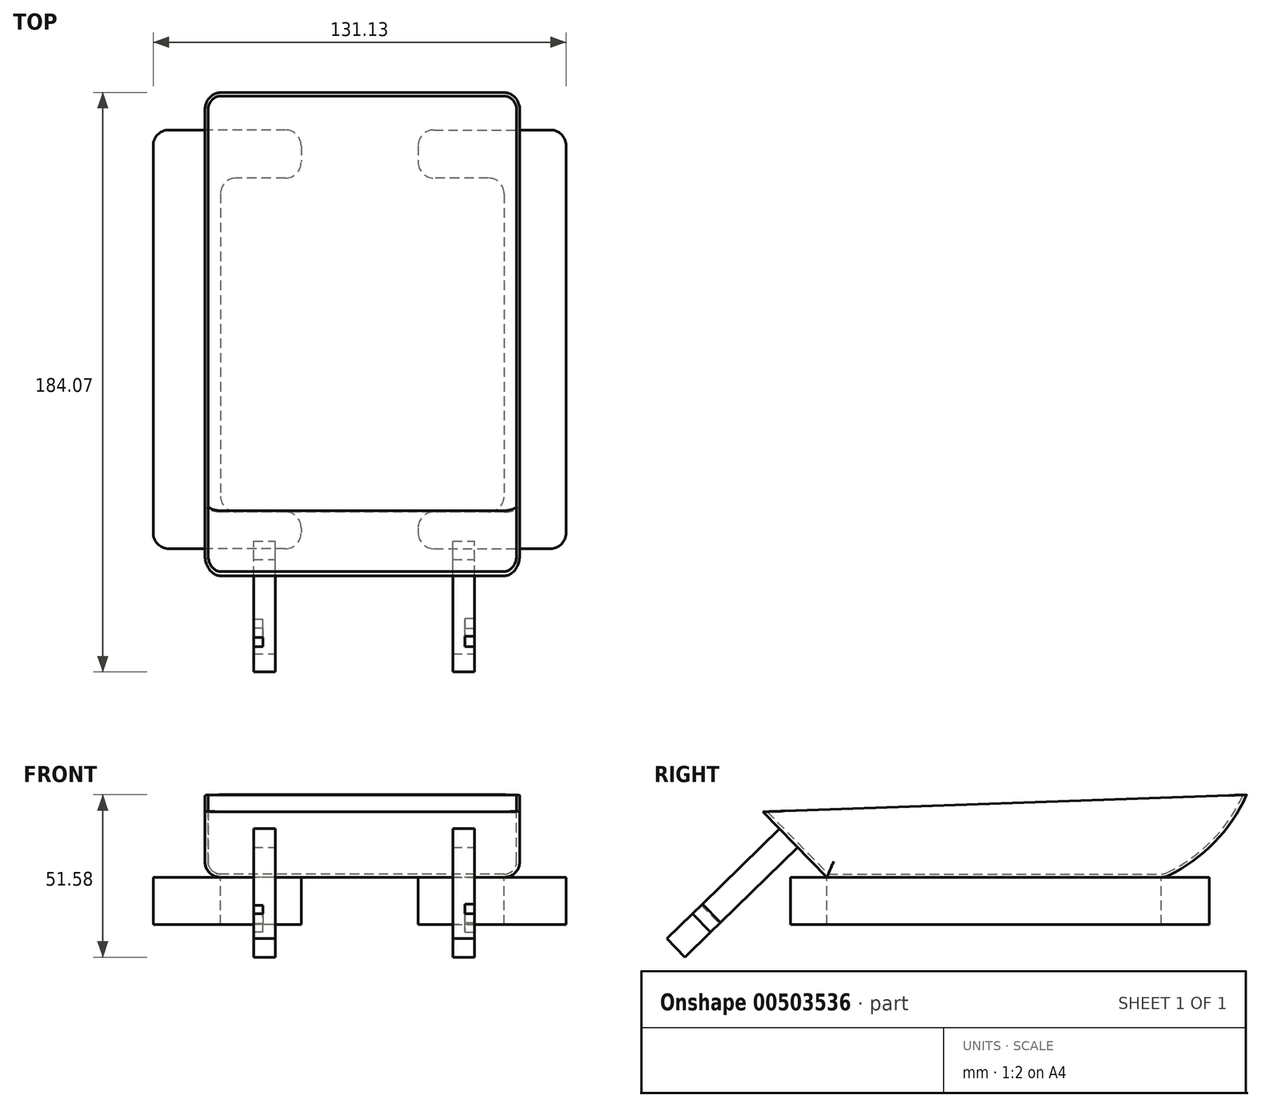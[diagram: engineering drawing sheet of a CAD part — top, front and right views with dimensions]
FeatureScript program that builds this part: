
annotation { "Feature Type Name" : "Feature", "Feature Type Description" : "" }
export const myFeature = defineFeature(function(context is Context, id is Id, definition is map)
    precondition{}
    {
        {
            var Q0;
            Q0=qCreatedBy(makeId("Right.planeOp"),FACE);
            var sketch = newSketch(context, id + "F0", { "sketchPlane" : qUnion([Q0])});
            skLineSegment(sketch, "E0", {"start": v(43.87, 0) * mm, "end": v(-62.22, 0) * mm});
            skLineSegment(sketch, "E1", {"start": v(-62.22, 0) * mm, "end": v(-82.51, 20.8) * mm});
            skArc(sketch, "E2", {"start": v(46.03, 0.49) * mm, "mid": v(60.82, 11.11) * mm, "end": v(71.02, 26.2) * mm});
            skPoint(sketch, "E3.visualSharp", {"position": v(44.98, 0) * mm});
            skArc(sketch, "E3.filletArc", {"start": v(43.87, 0) * mm, "mid": v(44.98, 0.12) * mm, "end": v(46.03, 0.49) * mm});
            skPoint(sketch, "E4.start.orphan", {"position": v(43.87, 3.2) * mm});
            skLineSegment(sketch, "E5", {"start": v(-82.51, 20.8) * mm, "end": v(71.02, 26.2) * mm});
            skSolve(sketch);
        }
        {
            var Q0;
            Q0=makeQuery(id+"F0.imprint","IMPRINT",FACE,{"disambiguationData":[TD([[makeQuery(id+"F0.imprint","IMPRINT",EDGE,{"derivedFrom":sQuery(id+"F0.wireOp",EDGE,"E0")}),-1.0]])]});
            extrude(context, id + "F1", {"entities" : qUnion([Q0]), "depth" : 100 * mm});
        }
        {
            var Q0;
            Q0=makeQuery(id+"F1.opExtrude","CAP_EDGE",EDGE,{"disambiguationData":[OSD([sQuery(id+"F0.wireOp",EDGE,"E1")])],"isStart":false});
            var Q1;
            Q1=makeQuery(id+"F1.opExtrude","CAP_EDGE",EDGE,{"disambiguationData":[OSD([sQuery(id+"F0.wireOp",EDGE,"E0")])],"isStart":false});
            var Q2;
            Q2=makeQuery(id+"F1.opExtrude","CAP_EDGE",EDGE,{"disambiguationData":[OSD([sQuery(id+"F0.wireOp",EDGE,"E2")])],"isStart":true});
            var Q3;
            Q3=makeQuery(id+"F1.opExtrude","CAP_EDGE",EDGE,{"disambiguationData":[OSD([sQuery(id+"F0.wireOp",EDGE,"E1")])],"isStart":true});
            fillet(context, id + "F2", {"entities" : qUnion([Q0, Q1, Q2, Q3]), "radius" : 5 * mm, "tangentPropagation" : true, "allowEdgeOverflow" : false});
        }
        {
            var Q0;
            Q0=makeQuery(id+"F1.opExtrude","SWEPT_FACE",FACE,{"disambiguationData":[OSD([sQuery(id+"F0.wireOp",EDGE,"E5")])]});
            shell(context, id + "F3", {"entities" : qUnion([Q0]), "thickness" : 1 * mm});
        }
        {
            var Q0;
            Q0=makeQuery(id+"F1.opExtrude","SWEPT_FACE",FACE,{"disambiguationData":[OSD([sQuery(id+"F0.wireOp",EDGE,"E0")])]});
            var sketch = newSketch(context, id + "F4", { "sketchPlane" : qUnion([Q0])});
            skLineSegment(sketch, "E6.bottom", {"start": v(30.57, -59.13) * mm, "end": v(-16.43, -59.13) * mm});
            skLineSegment(sketch, "E6.top", {"start": v(30.57, 73.87) * mm, "end": v(-16.43, 73.87) * mm});
            skLineSegment(sketch, "E6.left", {"start": v(30.57, -59.13) * mm, "end": v(30.57, 73.87) * mm});
            skLineSegment(sketch, "E6.right", {"start": v(-16.43, -59.13) * mm, "end": v(-16.43, 73.87) * mm});
            skLineSegment(sketch, "E7.bottom", {"start": v(67.7, -59.13) * mm, "end": v(114.7, -59.13) * mm});
            skLineSegment(sketch, "E7.top", {"start": v(67.7, 73.87) * mm, "end": v(114.7, 73.87) * mm});
            skLineSegment(sketch, "E7.left", {"start": v(67.7, -59.13) * mm, "end": v(67.7, 73.87) * mm});
            skLineSegment(sketch, "E7.right", {"start": v(114.7, -59.13) * mm, "end": v(114.7, 73.87) * mm});
            skSolve(sketch);
        }
        {
            var Q0;
            {var subQ5=sQuery(id+"F4.wireOp",EDGE,"E7.bottom");Q0=makeQuery(id+"F4.imprint","IMPRINT",FACE,{"disambiguationData":[TD([[makeQuery(id+"F4.imprint","IMPRINT",EDGE,{"derivedFrom":subQ5}),1.0]])]});}
            var Q1;
            {var subQ5=sQuery(id+"F4.wireOp",EDGE,"E6.bottom");Q1=makeQuery(id+"F4.imprint","IMPRINT",FACE,{"disambiguationData":[TD([[makeQuery(id+"F4.imprint","IMPRINT",EDGE,{"derivedFrom":subQ5}),-1.0]])]});}
            extrude(context, id + "F5", {"entities" : qUnion([Q0, Q1]), "depth" : 15 * mm});
        }
        {
            var Q0;
            Q0=makeQuery(id+"F5.opExtrude","SWEPT_EDGE",EDGE,{"disambiguationData":[OSD([sQuery(id+"F4.wireOp",EDGE,"E7.top"),sQuery(id+"F4.wireOp",EDGE,"E7.right")])]});
            var Q1;
            Q1=makeQuery(id+"F5.opExtrude","SWEPT_EDGE",EDGE,{"disambiguationData":[OSD([sQuery(id+"F4.wireOp",EDGE,"E7.bottom"),sQuery(id+"F4.wireOp",EDGE,"E7.right")])]});
            var Q2;
            Q2=makeQuery(id+"F5.opExtrude","SWEPT_EDGE",EDGE,{"disambiguationData":[OSD([sQuery(id+"F4.wireOp",EDGE,"E6.top"),sQuery(id+"F4.wireOp",EDGE,"E6.right")])]});
            var Q3;
            Q3=makeQuery(id+"F5.opExtrude","SWEPT_EDGE",EDGE,{"disambiguationData":[OSD([sQuery(id+"F4.wireOp",EDGE,"E6.bottom"),sQuery(id+"F4.wireOp",EDGE,"E6.right")])]});
            var Q4;
            Q4=makeQuery(id+"F5.opExtrude","SWEPT_EDGE",EDGE,{"disambiguationData":[OSD([sQuery(id+"F4.wireOp",EDGE,"E6.bottom"),sQuery(id+"F4.wireOp",EDGE,"E6.left")])]});
            var Q5;
            Q5=makeQuery(id+"F5.opExtrude","SWEPT_EDGE",EDGE,{"disambiguationData":[OSD([sQuery(id+"F4.wireOp",EDGE,"E7.bottom"),sQuery(id+"F4.wireOp",EDGE,"E7.left")])]});
            var Q6;
            Q6=makeQuery(id+"F5.opExtrude","SWEPT_EDGE",EDGE,{"disambiguationData":[OSD([sQuery(id+"F4.wireOp",EDGE,"E6.top"),sQuery(id+"F4.wireOp",EDGE,"E6.left")])]});
            var Q7;
            Q7=makeQuery(id+"F5.opExtrude","SWEPT_EDGE",EDGE,{"disambiguationData":[OSD([sQuery(id+"F4.wireOp",EDGE,"E7.top"),sQuery(id+"F4.wireOp",EDGE,"E7.left")])]});
            var Q8;
            {var subQ0=sQuery(id+"F0.wireOp",EDGE,"E0");var subQ1=sQuery(id+"F0.wireOp",EDGE,"E1");Q8=makeQuery(id+"F5.opExtrude","SWEPT_EDGE",EDGE,{"disambiguationData":[OSD([subQ0,subQ1]),TDD([makeQuery(id+"F4.imprint","INTERSECT",VERTEX,{"derivedFrom":[makeQuery(id+"F1.opExtrude","SWEPT_EDGE",EDGE,{"disambiguationData":[OSD([subQ0,subQ1])]}),makeQuery(id+"F2.opFillet","BLEND_EDGE",EDGE,{"blendedFrom":[makeQuery(id+"F1.opExtrude","CAP_EDGE",EDGE,{"disambiguationData":[OSD([subQ0])],"isStart":true}),makeQuery(id+"F1.opExtrude","SWEPT_FACE",FACE,{"disambiguationData":[OSD([subQ0])]})],"blendedInto":[makeQuery(id+"F1.opExtrude","SWEPT_FACE",FACE,{"disambiguationData":[OSD([subQ0])]})]})]})])]});}
            var Q9;
            {var subQ0=sQuery(id+"F0.wireOp",EDGE,"E0");var subQ1=sQuery(id+"F0.wireOp",EDGE,"E1");Q9=makeQuery(id+"F5.opExtrude","SWEPT_EDGE",EDGE,{"disambiguationData":[OSD([subQ0,subQ1]),TDD([makeQuery(id+"F4.imprint","INTERSECT",VERTEX,{"derivedFrom":[makeQuery(id+"F1.opExtrude","SWEPT_EDGE",EDGE,{"disambiguationData":[OSD([subQ0,subQ1])]}),makeQuery(id+"F2.opFillet","BLEND_EDGE",EDGE,{"blendedFrom":[makeQuery(id+"F1.opExtrude","CAP_EDGE",EDGE,{"disambiguationData":[OSD([subQ0])],"isStart":false}),makeQuery(id+"F1.opExtrude","SWEPT_FACE",FACE,{"disambiguationData":[OSD([subQ0])]})],"blendedInto":[makeQuery(id+"F1.opExtrude","SWEPT_FACE",FACE,{"disambiguationData":[OSD([subQ0])]})]})]})])]});}
            var Q10;
            {var subQ0=sQuery(id+"F0.wireOp",EDGE,"E0");var subQ1=sQuery(id+"F0.wireOp",EDGE,"E3.filletArc");Q10=makeQuery(id+"F5.opExtrude","SWEPT_EDGE",EDGE,{"disambiguationData":[OSD([subQ0,subQ1]),TDD([makeQuery(id+"F4.imprint","INTERSECT",VERTEX,{"derivedFrom":[makeQuery(id+"F1.opExtrude","SWEPT_EDGE",EDGE,{"disambiguationData":[OSD([subQ0,subQ1])]}),makeQuery(id+"F2.opFillet","BLEND_EDGE",EDGE,{"blendedFrom":[makeQuery(id+"F1.opExtrude","CAP_EDGE",EDGE,{"disambiguationData":[OSD([subQ0])],"isStart":true}),makeQuery(id+"F1.opExtrude","SWEPT_FACE",FACE,{"disambiguationData":[OSD([subQ0])]})],"blendedInto":[makeQuery(id+"F1.opExtrude","SWEPT_FACE",FACE,{"disambiguationData":[OSD([subQ0])]})]})]})])]});}
            var Q11;
            {var subQ0=sQuery(id+"F0.wireOp",EDGE,"E0");var subQ1=sQuery(id+"F0.wireOp",EDGE,"E3.filletArc");Q11=makeQuery(id+"F5.opExtrude","SWEPT_EDGE",EDGE,{"disambiguationData":[OSD([subQ0,subQ1]),TDD([makeQuery(id+"F4.imprint","INTERSECT",VERTEX,{"derivedFrom":[makeQuery(id+"F1.opExtrude","SWEPT_EDGE",EDGE,{"disambiguationData":[OSD([subQ0,subQ1])]}),makeQuery(id+"F2.opFillet","BLEND_EDGE",EDGE,{"blendedFrom":[makeQuery(id+"F1.opExtrude","CAP_EDGE",EDGE,{"disambiguationData":[OSD([subQ0])],"isStart":false}),makeQuery(id+"F1.opExtrude","SWEPT_FACE",FACE,{"disambiguationData":[OSD([subQ0])]})],"blendedInto":[makeQuery(id+"F1.opExtrude","SWEPT_FACE",FACE,{"disambiguationData":[OSD([subQ0])]})]})]})])]});}
            var Q12;
            Q12=makeQuery(id+"F5.opExtrude","SWEPT_EDGE",EDGE,{"disambiguationData":[OSD([sQuery(id+"F0.wireOp",EDGE,"E0"),sQuery(id+"F0.wireOp",EDGE,"E3.filletArc"),sQuery(id+"F4.wireOp",EDGE,"E7.left")])]});
            var Q13;
            Q13=makeQuery(id+"F5.opExtrude","SWEPT_EDGE",EDGE,{"disambiguationData":[OSD([sQuery(id+"F0.wireOp",EDGE,"E0"),sQuery(id+"F0.wireOp",EDGE,"E3.filletArc"),sQuery(id+"F4.wireOp",EDGE,"E6.left")])]});
            var Q14;
            Q14=makeQuery(id+"F5.opExtrude","SWEPT_EDGE",EDGE,{"disambiguationData":[OSD([sQuery(id+"F0.wireOp",EDGE,"E0"),sQuery(id+"F0.wireOp",EDGE,"E1"),sQuery(id+"F4.wireOp",EDGE,"E6.left")])]});
            var Q15;
            Q15=makeQuery(id+"F5.opExtrude","SWEPT_EDGE",EDGE,{"disambiguationData":[OSD([sQuery(id+"F0.wireOp",EDGE,"E0"),sQuery(id+"F0.wireOp",EDGE,"E1"),sQuery(id+"F4.wireOp",EDGE,"E7.left")])]});
            fillet(context, id + "F6", {"entities" : qUnion([Q0, Q1, Q2, Q3, Q4, Q5, Q6, Q7, Q8, Q9, Q10, Q11, Q12, Q13, Q14, Q15]), "radius" : 5 * mm, "tangentPropagation" : true, "allowEdgeOverflow" : false});
        }
        {
            var Q0;
            Q0=makeQuery(id+"F1.opExtrude","SWEPT_FACE",FACE,{"disambiguationData":[OSD([sQuery(id+"F0.wireOp",EDGE,"E1")])]});
            var sketch = newSketch(context, id + "F7", { "sketchPlane" : qUnion([Q0])});
            skLineSegment(sketch, "E8.bottom", {"start": v(15.46, 64.99) * mm, "end": v(22.3, 64.99) * mm});
            skLineSegment(sketch, "E8.top", {"start": v(15.46, 56.78) * mm, "end": v(22.3, 56.78) * mm});
            skLineSegment(sketch, "E8.left", {"start": v(15.46, 64.99) * mm, "end": v(15.46, 56.78) * mm});
            skLineSegment(sketch, "E8.right", {"start": v(22.3, 64.99) * mm, "end": v(22.3, 56.78) * mm});
            skPoint(sketch, "E8.middle", {"position": v(18.88, 60.89) * mm});
            skLineSegment(sketch, "E9.bottom", {"start": v(78.72, 64.99) * mm, "end": v(85.56, 64.99) * mm});
            skLineSegment(sketch, "E9.top", {"start": v(78.72, 56.78) * mm, "end": v(85.56, 56.78) * mm});
            skLineSegment(sketch, "E9.left", {"start": v(78.72, 64.99) * mm, "end": v(78.72, 56.78) * mm});
            skLineSegment(sketch, "E9.right", {"start": v(85.56, 64.99) * mm, "end": v(85.56, 56.78) * mm});
            skPoint(sketch, "E9.middle", {"position": v(82.14, 60.89) * mm});
            skSolve(sketch);
        }
        {
            var Q0;
            Q0=makeQuery(id+"F7.imprint","IMPRINT",FACE,{"disambiguationData":[TD([[makeQuery(id+"F7.imprint","IMPRINT",EDGE,{"derivedFrom":sQuery(id+"F7.wireOp",EDGE,"E8.bottom")}),-1.0]])]});
            var Q1;
            Q1=makeQuery(id+"F7.imprint","IMPRINT",FACE,{"disambiguationData":[TD([[makeQuery(id+"F7.imprint","IMPRINT",EDGE,{"derivedFrom":sQuery(id+"F7.wireOp",EDGE,"E9.bottom")}),-1.0]])]});
            extrude(context, id + "F8", {"entities" : qUnion([Q0, Q1]), "operationType" : NewBodyOperationType.ADD, "depth" : 50 * mm});
        }
        {
            var Q0;
            Q0=makeQuery(id+"F8.opExtrude","SWEPT_FACE",FACE,{"disambiguationData":[OSD([sQuery(id+"F7.wireOp",EDGE,"E9.right")])]});
            var sketch = newSketch(context, id + "F9", { "sketchPlane" : qUnion([Q0])});
            skLineSegment(sketch, "E10", {"start": v(-116.26, 0) * mm, "end": v(-91.52, -25.36) * mm});
            skLineSegment(sketch, "E11", {"start": v(-91.52, -25.36) * mm, "end": v(-88.32, -22.24) * mm});
            skLineSegment(sketch, "E12", {"start": v(-88.32, -22.24) * mm, "end": v(-111.31, 1.32) * mm});
            skLineSegment(sketch, "E13", {"start": v(-111.31, 1.32) * mm, "end": v(-116.26, 0) * mm});
            skSolve(sketch);
        }
        {
            var Q0;
            {var subQ0=sQuery(id+"F9.wireOp",EDGE,"E10");var subQ1=sQuery(id+"F7.wireOp",EDGE,"E9.right");var subQ2=makeQuery(id+"F8.opExtrude","SWEPT_EDGE",EDGE,{"disambiguationData":[OSD([sQuery(id+"F7.wireOp",EDGE,"E9.bottom"),subQ1])]});var subQ3=makeQuery(id+"F9.imprint","INTERSECT",VERTEX,{"derivedFrom":[subQ2,subQ0]});Q0=makeQuery(id+"F9.imprint","IMPRINT",FACE,{"disambiguationData":[TD([[makeQuery(id+"F9.imprint","IMPRINT",EDGE,{"disambiguationData":[TD([[subQ3,-1.0]])],"derivedFrom":subQ0}),1.0]])]});}
            extrude(context, id + "F10", {"entities" : qUnion([Q0]), "operationType" : NewBodyOperationType.REMOVE, "oppositeDirection" : true, "depth" : 3 * mm});
        }
        {
            var Q0;
            Q0=makeQuery(id+"F8.opExtrude","SWEPT_FACE",FACE,{"disambiguationData":[OSD([sQuery(id+"F7.wireOp",EDGE,"E8.left")])]});
            var sketch = newSketch(context, id + "F11", { "sketchPlane" : qUnion([Q0])});
            skLineSegment(sketch, "E14", {"start": v(105.17, -5.76) * mm, "end": v(92.83, -18.4) * mm});
            skLineSegment(sketch, "E15", {"start": v(92.83, -18.4) * mm, "end": v(95.64, -21.14) * mm});
            skLineSegment(sketch, "E16", {"start": v(95.64, -21.14) * mm, "end": v(107.36, -9.12) * mm});
            skLineSegment(sketch, "E17", {"start": v(107.36, -9.12) * mm, "end": v(105.17, -5.76) * mm});
            skSolve(sketch);
        }
        {
            var Q0;
            {var subQ0=sQuery(id+"F11.wireOp",EDGE,"E14");var subQ1=sQuery(id+"F7.wireOp",EDGE,"E8.left");var subQ2=makeQuery(id+"F8.opExtrude","SWEPT_EDGE",EDGE,{"disambiguationData":[OSD([sQuery(id+"F7.wireOp",EDGE,"E8.bottom"),subQ1])]});var subQ3=makeQuery(id+"F11.imprint","INTERSECT",VERTEX,{"derivedFrom":[subQ2,subQ0]});Q0=makeQuery(id+"F11.imprint","IMPRINT",FACE,{"disambiguationData":[TD([[makeQuery(id+"F11.imprint","IMPRINT",EDGE,{"disambiguationData":[TD([[subQ3,-1.0]])],"derivedFrom":subQ0}),1.0]])]});}
            extrude(context, id + "F12", {"entities" : qUnion([Q0]), "operationType" : NewBodyOperationType.REMOVE, "oppositeDirection" : true, "depth" : 3 * mm});
        }
    });
